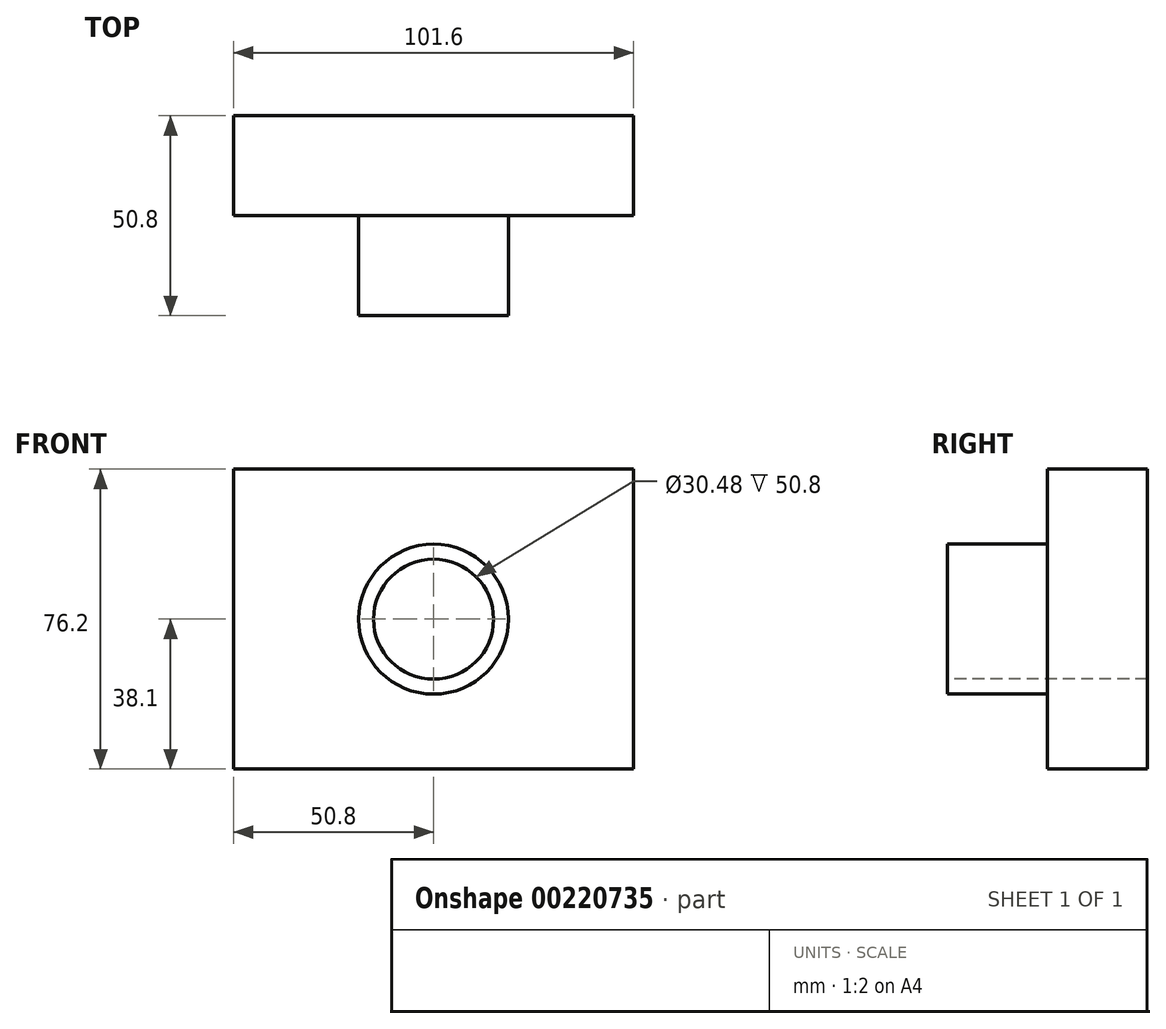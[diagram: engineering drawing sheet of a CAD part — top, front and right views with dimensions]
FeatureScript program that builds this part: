
annotation { "Feature Type Name" : "Feature", "Feature Type Description" : "" }
export const myFeature = defineFeature(function(context is Context, id is Id, definition is map)
    precondition{}
    {
        {
            var Q0;
            Q0=qCreatedBy(makeId("Front.planeOp"),FACE);
            var sketch = newSketch(context, id + "F0", { "sketchPlane" : qUnion([Q0])});
            skLineSegment(sketch, "E0.bottom", {"start": v(50.8, -38.1) * mm, "end": v(-50.8, -38.1) * mm});
            skLineSegment(sketch, "E0.top", {"start": v(50.8, 38.1) * mm, "end": v(-50.8, 38.1) * mm});
            skLineSegment(sketch, "E0.left", {"start": v(50.8, -38.1) * mm, "end": v(50.8, 38.1) * mm});
            skLineSegment(sketch, "E0.right", {"start": v(-50.8, -38.1) * mm, "end": v(-50.8, 38.1) * mm});
            skPoint(sketch, "E0.middle", {"position": v(0, 0) * mm});
            skSolve(sketch);
        }
        {
            var Q0;
            Q0 = qSketchRegion(id + "F0", true);
            extrude(context, id + "F1", {"entities" : qUnion([Q0]), "depth" : 25.4 * mm});
        }
        {
            var Q0;
            Q0=makeQuery(id+"F1.opExtrude","CAP_FACE",FACE,{"disambiguationData":[OSD([sQuery(id+"F0.wireOp",EDGE,"E0.bottom"),sQuery(id+"F0.wireOp",EDGE,"E0.top"),sQuery(id+"F0.wireOp",EDGE,"E0.left"),sQuery(id+"F0.wireOp",EDGE,"E0.right")])],"isStart":false});
            var sketch = newSketch(context, id + "F2", { "sketchPlane" : qUnion([Q0])});
            skCircle(sketch, "E1", {"center": v(0, 0) * mm, "radius": 19.05 * mm});
            skSolve(sketch);
        }
        {
            var Q0;
            Q0=makeQuery(id+"F2.imprint","IMPRINT",FACE,{"disambiguationData":[TD([[makeQuery(id+"F2.imprint","IMPRINT",EDGE,{"derivedFrom":sQuery(id+"F2.wireOp",EDGE,"E1")}),1.0]])]});
            extrude(context, id + "F3", {"entities" : qUnion([Q0]), "operationType" : NewBodyOperationType.ADD, "depth" : 25.4 * mm});
        }
        {
            var Q0;
            Q0=makeQuery(id+"F3.opExtrude","CAP_FACE",FACE,{"disambiguationData":[OSD([sQuery(id+"F2.wireOp",EDGE,"E1")])],"isStart":false});
            var sketch = newSketch(context, id + "F4", { "sketchPlane" : qUnion([Q0])});
            skCircle(sketch, "E2", {"center": v(0, 0) * mm, "radius": 15.24 * mm});
            skSolve(sketch);
        }
        {
            var Q0;
            Q0 = qSketchRegion(id + "F4", true);
            extrude(context, id + "F5", {"entities" : qUnion([Q0]), "operationType" : NewBodyOperationType.REMOVE, "oppositeDirection" : true, "depth" : 76.2 * mm});
        }
    });
